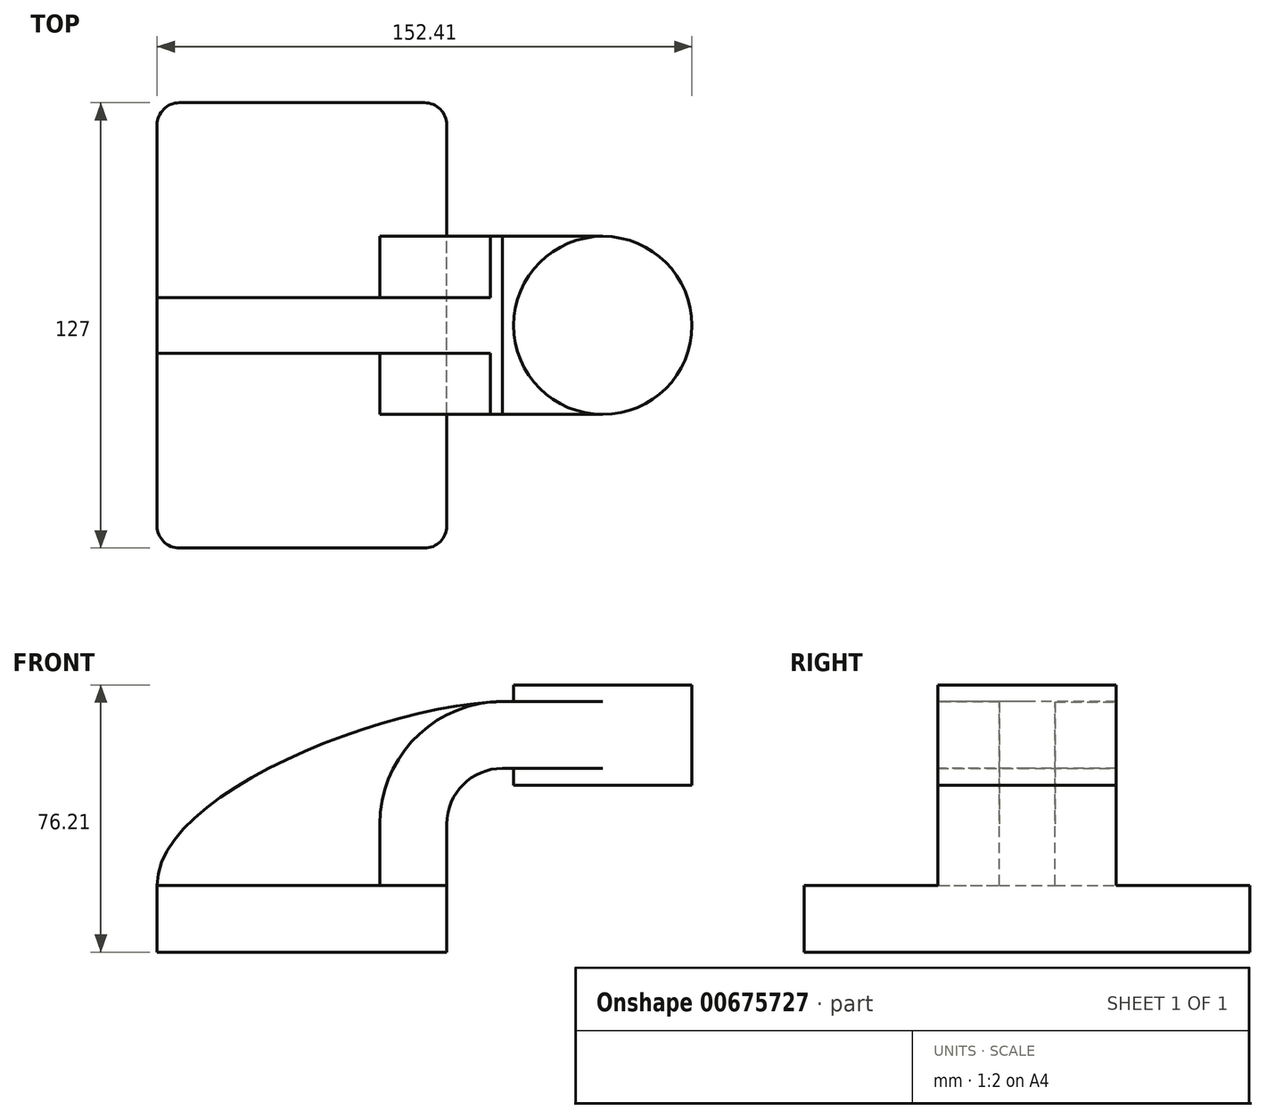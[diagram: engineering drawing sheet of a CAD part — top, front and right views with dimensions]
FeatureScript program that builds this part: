
annotation { "Feature Type Name" : "Feature", "Feature Type Description" : "" }
export const myFeature = defineFeature(function(context is Context, id is Id, definition is map)
    precondition{}
    {
        {
            var Q0;
            Q0=qCreatedBy(makeId("Front.planeOp"),FACE);
            var sketch = newSketch(context, id + "F0", { "sketchPlane" : qUnion([Q0])});
            skLineSegment(sketch, "E0.bottom", {"start": v(41.28, -9.52) * mm, "end": v(-41.28, -9.52) * mm});
            skLineSegment(sketch, "E0.top", {"start": v(41.28, 9.53) * mm, "end": v(-41.28, 9.53) * mm});
            skLineSegment(sketch, "E0.left", {"start": v(41.28, -9.52) * mm, "end": v(41.28, 9.53) * mm});
            skLineSegment(sketch, "E0.right", {"start": v(-41.28, -9.52) * mm, "end": v(-41.28, 9.53) * mm});
            skPoint(sketch, "E0.middle", {"position": v(0, 0) * mm});
            skLineSegment(sketch, "E1.bottom", {"start": v(60.32, 38.1) * mm, "end": v(111.12, 38.1) * mm});
            skLineSegment(sketch, "E1.top", {"start": v(60.32, 66.68) * mm, "end": v(111.12, 66.68) * mm});
            skLineSegment(sketch, "E1.left", {"start": v(60.32, 38.1) * mm, "end": v(60.32, 66.68) * mm});
            skLineSegment(sketch, "E1.right", {"start": v(111.12, 38.1) * mm, "end": v(111.12, 66.68) * mm});
            skPoint(sketch, "E1.middle", {"position": v(85.72, 52.39) * mm});
            skLineSegment(sketch, "E2", {"start": v(41.28, 9.53) * mm, "end": v(41.28, 27) * mm});
            skArc(sketch, "E3", {"start": v(41.27, 27) * mm, "mid": v(45.92, 38.23) * mm, "end": v(57.15, 42.88) * mm});
            skLineSegment(sketch, "E4", {"start": v(57.15, 42.88) * mm, "end": v(85.72, 42.88) * mm});
            skLineSegment(sketch, "E5.0", {"start": v(57.15, 61.93) * mm, "end": v(85.72, 61.93) * mm});
            skArc(sketch, "E5.1", {"start": v(22.23, 27) * mm, "mid": v(32.45, 51.7) * mm, "end": v(57.15, 61.93) * mm});
            skLineSegment(sketch, "E5.2", {"start": v(22.22, 9.53) * mm, "end": v(22.22, 27) * mm});
            skLineSegment(sketch, "E6", {"start": v(85.72, 38.1) * mm, "end": v(85.72, 66.68) * mm});
            skFitSpline(sketch, "E7", {"points": [v(-41.28, 9.52) * mm, v(57.15, 61.93) * mm], "startDerivative": vector(-0.8, 77.5) * mm, "endDerivative": vector(103.4, 2.86) * mm});
            skSolve(sketch);
        }
        {
            var Q0;
            Q0=makeQuery(id+"F0.imprint","IMPRINT",FACE,{"disambiguationData":[TD([[makeQuery(id+"F0.imprint","IMPRINT",EDGE,{"derivedFrom":sQuery(id+"F0.wireOp",EDGE,"E0.bottom")}),-1.0]])]});
            extrude(context, id + "F1", {"entities" : qUnion([Q0]), "endBound" : BoundingType.SYMMETRIC, "depth" : 127 * mm, "offsetDistance" : 25.4 * mm});
        }
        {
            var Q0;
            {var subQ0=sQuery(id+"F0.wireOp",EDGE,"E2");Q0=makeQuery(id+"F0.imprint","IMPRINT",FACE,{"disambiguationData":[TD([[makeQuery(id+"F0.imprint","IMPRINT",EDGE,{"derivedFrom":subQ0}),1.0]])]});}
            var Q1;
            {var subQ0=sQuery(id+"F0.wireOp",EDGE,"E4");var subQ1=sQuery(id+"F0.wireOp",EDGE,"E1.left");var subQ2=makeQuery(id+"F0.imprint","INTERSECT",VERTEX,{"derivedFrom":[subQ1,subQ0]});Q1=makeQuery(id+"F0.imprint","IMPRINT",FACE,{"disambiguationData":[TD([[makeQuery(id+"F0.imprint","IMPRINT",EDGE,{"disambiguationData":[TD([[subQ2,-1.0]])],"derivedFrom":subQ1}),-1.0]])]});}
            extrude(context, id + "F2", {"entities" : qUnion([Q0, Q1]), "operationType" : NewBodyOperationType.ADD, "endBound" : BoundingType.SYMMETRIC, "depth" : 50.8 * mm, "offsetDistance" : 25.4 * mm});
        }
        {
            var Q0;
            {var subQ0=sQuery(id+"F0.wireOp",EDGE,"E5.2");Q0=makeQuery(id+"F0.imprint","IMPRINT",FACE,{"disambiguationData":[TD([[makeQuery(id+"F0.imprint","IMPRINT",EDGE,{"derivedFrom":subQ0}),1.0]])]});}
            extrude(context, id + "F3", {"entities" : qUnion([Q0]), "operationType" : NewBodyOperationType.ADD, "endBound" : BoundingType.SYMMETRIC, "depth" : 15.88 * mm, "offsetDistance" : 25.4 * mm});
        }
        {
            var Q0;
            {var subQ3=sQuery(id+"F0.wireOp",EDGE,"E1.right");Q0=makeQuery(id+"F0.imprint","IMPRINT",FACE,{"disambiguationData":[TD([[makeQuery(id+"F0.imprint","IMPRINT",EDGE,{"derivedFrom":subQ3}),1.0]])]});}
            var Q1;
            Q1=sQuery(id+"F0.wireOp",EDGE,"E6");
            revolve(context, id + "F4", {"operationType" : NewBodyOperationType.ADD, "surfaceOperationType" : NewSurfaceOperationType.NEW, "entities" : qUnion([Q0]), "axis" : qUnion([Q1]), "revolveType" : RevolveType.FULL});
        }
        {
            var Q0;
            Q0=makeQuery(id+"F1.opExtrude","CAP_EDGE",EDGE,{"disambiguationData":[OSD([sQuery(id+"F0.wireOp",EDGE,"E0.right")])],"isStart":false});
            var Q1;
            Q1=makeQuery(id+"F1.opExtrude","CAP_EDGE",EDGE,{"disambiguationData":[OSD([sQuery(id+"F0.wireOp",EDGE,"E0.left")])],"isStart":false});
            var Q2;
            Q2=makeQuery(id+"F1.opExtrude","CAP_EDGE",EDGE,{"disambiguationData":[OSD([sQuery(id+"F0.wireOp",EDGE,"E0.left")])],"isStart":true});
            var Q3;
            Q3=makeQuery(id+"F1.opExtrude","CAP_EDGE",EDGE,{"disambiguationData":[OSD([sQuery(id+"F0.wireOp",EDGE,"E0.right")])],"isStart":true});
            fillet(context, id + "F5", {"entities" : qUnion([Q0, Q1, Q2, Q3]), "tangentPropagation" : true, "radius" : 6.35 * mm, "defaultsChanged" : true, "vertexSettings" : [], "allowEdgeOverflow" : false});
        }
    });
